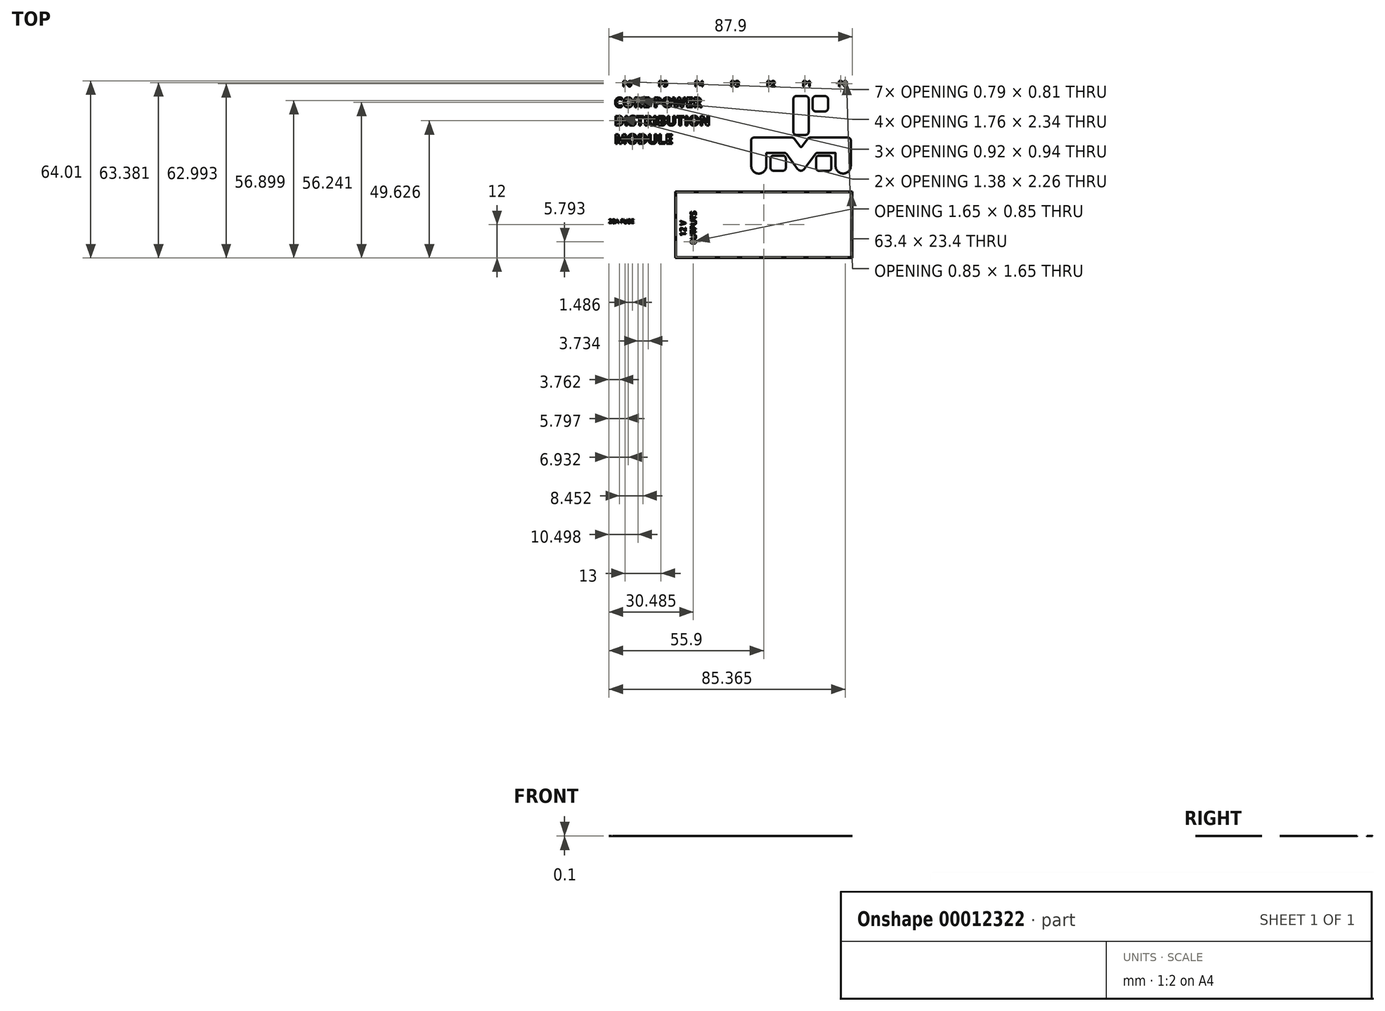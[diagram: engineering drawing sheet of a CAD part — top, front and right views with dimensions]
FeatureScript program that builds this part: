
annotation { "Feature Type Name" : "Feature", "Feature Type Description" : "" }
export const myFeature = defineFeature(function(context is Context, id is Id, definition is map)
    precondition{}
    {
        {
            var Q0;
            Q0=qCreatedBy(makeId("Top.planeOp"),FACE);
            var sketch = newSketch(context, id + "F0", { "sketchPlane" : qUnion([Q0])});
            skText(sketch, "E0", { "text": "P6", "fontName": "OpenSans-Regular.ttf"});
            skPoint(sketch, "E1", {"position": v(0, -2) * mm});
            skPoint(sketch, "E2.1.0.0", {"position": v(13, -2) * mm});
            skPoint(sketch, "E2.2.0.0", {"position": v(26, -2) * mm});
            skPoint(sketch, "E2.3.0.0", {"position": v(39, -2) * mm});
            skPoint(sketch, "E2.4.0.0", {"position": v(52, -2) * mm});
            skPoint(sketch, "E2.5.0.0", {"position": v(65, -2) * mm});
            skPoint(sketch, "E2.6.0.0", {"position": v(78, -2) * mm});
            skLineSegment(sketch, "E2.direction1", {"start": v(0, -2) * mm, "end": v(13, -2) * mm, "construction": true});
            skText(sketch, "E3", { "text": "P5", "fontName": "OpenSans-Regular.ttf"});
            skText(sketch, "E4", { "text": "P4", "fontName": "OpenSans-Regular.ttf"});
            skText(sketch, "E5", { "text": "P3", "fontName": "OpenSans-Regular.ttf"});
            skText(sketch, "E6", { "text": "P2", "fontName": "OpenSans-Regular.ttf"});
            skText(sketch, "E7", { "text": "P1", "fontName": "OpenSans-Regular.ttf"});
            skText(sketch, "E8", { "text": "P0", "fontName": "OpenSans-Regular.ttf"});
            skText(sketch, "E9", { "text": "CORE POWER\nDISTRIBUTION\nMODULE", "fontName": "OpenSans-Bold.ttf"});
            skLineSegment(sketch, "E10.bottom", {"start": v(62.75, -5.5) * mm, "end": v(66.25, -5.5) * mm});
            skLineSegment(sketch, "E10.top", {"start": v(62.75, -19.5) * mm, "end": v(66.25, -19.5) * mm});
            skLineSegment(sketch, "E10.left", {"start": v(61.75, -6.5) * mm, "end": v(61.75, -18.5) * mm});
            skLineSegment(sketch, "E10.right", {"start": v(67.25, -6.5) * mm, "end": v(67.25, -18.5) * mm});
            skLineSegment(sketch, "E11.bottom", {"start": v(69.75, -5.5) * mm, "end": v(73.25, -5.5) * mm});
            skLineSegment(sketch, "E11.top", {"start": v(69.75, -11) * mm, "end": v(73.25, -11) * mm});
            skLineSegment(sketch, "E11.left", {"start": v(68.75, -6.5) * mm, "end": v(68.75, -10) * mm});
            skLineSegment(sketch, "E11.right", {"start": v(74.25, -6.5) * mm, "end": v(74.25, -10) * mm});
            skLineSegment(sketch, "E12", {"start": v(64.5, -19.5) * mm, "end": v(64.5, -33.5) * mm, "construction": true});
            skLineSegment(sketch, "E13", {"start": v(63.3, -31.86) * mm, "end": v(59.27, -26.4) * mm});
            skLineSegment(sketch, "E14", {"start": v(58.47, -26) * mm, "end": v(52.1, -26) * mm});
            skLineSegment(sketch, "E15", {"start": v(52, -26.1) * mm, "end": v(52, -30.75) * mm});
            skLineSegment(sketch, "E16.0", {"start": v(46.5, -21.5) * mm, "end": v(46.5, -30.75) * mm});
            skLineSegment(sketch, "E16.1", {"start": v(61.24, -20.5) * mm, "end": v(47.5, -20.5) * mm});
            skLineSegment(sketch, "E16.2", {"start": v(64.1, -23.68) * mm, "end": v(62.05, -20.9) * mm});
            skLineSegment(sketch, "E17", {"start": v(49.25, -33.5) * mm, "end": v(49.25, -33.5) * mm});
            skPoint(sketch, "E18.orphan", {"position": v(52, -33.5) * mm});
            skPoint(sketch, "E19.visualSharp", {"position": v(46.5, -33.5) * mm});
            skArc(sketch, "E19.filletArc", {"start": v(46.5, -30.75) * mm, "mid": v(47.3, -32.7) * mm, "end": v(49.25, -33.5) * mm});
            skArc(sketch, "E20.filletArc", {"start": v(49.25, -33.5) * mm, "mid": v(51.2, -32.7) * mm, "end": v(52, -30.75) * mm});
            skLineSegment(sketch, "E21.right", {"start": v(59, -28) * mm, "end": v(59, -31.5) * mm});
            skLineSegment(sketch, "E21.left", {"start": v(53.5, -28) * mm, "end": v(53.5, -31.5) * mm});
            skLineSegment(sketch, "E21.top", {"start": v(54.5, -32.5) * mm, "end": v(58, -32.5) * mm});
            skLineSegment(sketch, "E21.bottom", {"start": v(54.5, -27) * mm, "end": v(58, -27) * mm});
            skPoint(sketch, "E22.0.MirrorP", {"position": v(77, -33.5) * mm});
            skLineSegment(sketch, "E22.1.MirrorCS", {"start": v(74.5, -27) * mm, "end": v(71, -27) * mm});
            skPoint(sketch, "E22.2.MirrorP", {"position": v(82.5, -33.5) * mm});
            skLineSegment(sketch, "E22.3.MirrorCS", {"start": v(70, -28) * mm, "end": v(70, -31.5) * mm});
            skLineSegment(sketch, "E22.4.MirrorCS", {"start": v(75.5, -28) * mm, "end": v(75.5, -31.5) * mm});
            skLineSegment(sketch, "E22.5.MirrorCS", {"start": v(74.5, -32.5) * mm, "end": v(71, -32.5) * mm});
            skLineSegment(sketch, "E22.6.MirrorCS", {"start": v(70.53, -26) * mm, "end": v(76.9, -26) * mm});
            skLineSegment(sketch, "E22.7.MirrorCS", {"start": v(77, -26.1) * mm, "end": v(77, -30.75) * mm});
            skArc(sketch, "E22.8.MirrorCS", {"start": v(79.75, -33.5) * mm, "mid": v(77.8, -32.7) * mm, "end": v(77, -30.75) * mm});
            skLineSegment(sketch, "E22.9.MirrorCS", {"start": v(79.75, -33.5) * mm, "end": v(79.75, -33.5) * mm});
            skLineSegment(sketch, "E22.10.MirrorCS", {"start": v(67.76, -20.5) * mm, "end": v(81.5, -20.5) * mm});
            skPoint(sketch, "E22.11.MirrorP", {"position": v(77, -33.5) * mm});
            skLineSegment(sketch, "E22.12.MirrorCS", {"start": v(64.9, -23.68) * mm, "end": v(66.95, -20.9) * mm});
            skArc(sketch, "E22.13.MirrorCS", {"start": v(82.5, -30.75) * mm, "mid": v(81.7, -32.7) * mm, "end": v(79.75, -33.5) * mm});
            skLineSegment(sketch, "E22.14.MirrorCS", {"start": v(65.7, -31.86) * mm, "end": v(69.73, -26.4) * mm});
            skLineSegment(sketch, "E22.15.MirrorCS", {"start": v(82.5, -21.5) * mm, "end": v(82.5, -30.75) * mm});
            skPoint(sketch, "E23.visualSharp", {"position": v(68.75, -5.5) * mm});
            skArc(sketch, "E23.filletArc", {"start": v(69.75, -5.5) * mm, "mid": v(69.04, -5.8) * mm, "end": v(68.75, -6.5) * mm});
            skPoint(sketch, "E24.visualSharp", {"position": v(74.25, -5.5) * mm});
            skArc(sketch, "E24.filletArc", {"start": v(74.25, -6.5) * mm, "mid": v(73.96, -5.8) * mm, "end": v(73.25, -5.5) * mm});
            skPoint(sketch, "E25.visualSharp", {"position": v(74.25, -11) * mm});
            skArc(sketch, "E25.filletArc", {"start": v(73.25, -11) * mm, "mid": v(73.96, -10.7) * mm, "end": v(74.25, -10) * mm});
            skPoint(sketch, "E26.visualSharp", {"position": v(68.75, -11) * mm});
            skArc(sketch, "E26.filletArc", {"start": v(68.75, -10) * mm, "mid": v(69.04, -10.7) * mm, "end": v(69.75, -11) * mm});
            skPoint(sketch, "E27.visualSharp", {"position": v(67.25, -5.5) * mm});
            skArc(sketch, "E27.filletArc", {"start": v(67.25, -6.5) * mm, "mid": v(66.96, -5.8) * mm, "end": v(66.25, -5.5) * mm});
            skPoint(sketch, "E28.visualSharp", {"position": v(61.75, -5.5) * mm});
            skArc(sketch, "E28.filletArc", {"start": v(62.75, -5.5) * mm, "mid": v(62.04, -5.8) * mm, "end": v(61.75, -6.5) * mm});
            skPoint(sketch, "E29.visualSharp", {"position": v(61.75, -19.5) * mm});
            skArc(sketch, "E29.filletArc", {"start": v(61.75, -18.5) * mm, "mid": v(62.04, -19.2) * mm, "end": v(62.75, -19.5) * mm});
            skPoint(sketch, "E30.visualSharp", {"position": v(67.25, -19.5) * mm});
            skArc(sketch, "E30.filletArc", {"start": v(66.25, -19.5) * mm, "mid": v(66.96, -19.2) * mm, "end": v(67.25, -18.5) * mm});
            skPoint(sketch, "E31.visualSharp", {"position": v(70, -32.5) * mm});
            skArc(sketch, "E31.filletArc", {"start": v(70, -31.5) * mm, "mid": v(70.3, -32.2) * mm, "end": v(71, -32.5) * mm});
            skPoint(sketch, "E32.visualSharp", {"position": v(75.5, -27) * mm});
            skArc(sketch, "E32.filletArc", {"start": v(75.5, -28) * mm, "mid": v(75.2, -27.3) * mm, "end": v(74.5, -27) * mm});
            skPoint(sketch, "E33.visualSharp", {"position": v(70, -27) * mm});
            skArc(sketch, "E33.filletArc", {"start": v(71, -27) * mm, "mid": v(70.3, -27.3) * mm, "end": v(70, -28) * mm});
            skPoint(sketch, "E34.visualSharp", {"position": v(75.5, -32.5) * mm});
            skArc(sketch, "E34.filletArc", {"start": v(74.5, -32.5) * mm, "mid": v(75.2, -32.2) * mm, "end": v(75.5, -31.5) * mm});
            skPoint(sketch, "E35.visualSharp", {"position": v(59, -32.5) * mm});
            skArc(sketch, "E35.filletArc", {"start": v(58, -32.5) * mm, "mid": v(58.7, -32.2) * mm, "end": v(59, -31.5) * mm});
            skPoint(sketch, "E36.visualSharp", {"position": v(59, -27) * mm});
            skArc(sketch, "E36.filletArc", {"start": v(59, -28) * mm, "mid": v(58.7, -27.3) * mm, "end": v(58, -27) * mm});
            skPoint(sketch, "E37.visualSharp", {"position": v(53.5, -27) * mm});
            skArc(sketch, "E37.filletArc", {"start": v(54.5, -27) * mm, "mid": v(53.8, -27.3) * mm, "end": v(53.5, -28) * mm});
            skPoint(sketch, "E38.visualSharp", {"position": v(53.5, -32.5) * mm});
            skArc(sketch, "E38.filletArc", {"start": v(53.5, -31.5) * mm, "mid": v(53.8, -32.2) * mm, "end": v(54.5, -32.5) * mm});
            skPoint(sketch, "E39.visualSharp", {"position": v(46.5, -20.5) * mm});
            skArc(sketch, "E39.filletArc", {"start": v(47.5, -20.5) * mm, "mid": v(46.8, -20.8) * mm, "end": v(46.5, -21.5) * mm});
            skPoint(sketch, "E40.visualSharp", {"position": v(82.5, -20.5) * mm});
            skArc(sketch, "E40.filletArc", {"start": v(82.5, -21.5) * mm, "mid": v(82.2, -20.8) * mm, "end": v(81.5, -20.5) * mm});
            skPoint(sketch, "E41.visualSharp", {"position": v(61.75, -20.5) * mm});
            skArc(sketch, "E41.filletArc", {"start": v(62.05, -20.9) * mm, "mid": v(61.7, -20.6) * mm, "end": v(61.24, -20.5) * mm});
            skPoint(sketch, "E42.visualSharp", {"position": v(67.25, -20.5) * mm});
            skArc(sketch, "E42.filletArc", {"start": v(67.76, -20.5) * mm, "mid": v(67.3, -20.6) * mm, "end": v(66.95, -20.9) * mm});
            skPoint(sketch, "E43.visualSharp", {"position": v(52, -26) * mm});
            skArc(sketch, "E43.filletArc", {"start": v(52.1, -26) * mm, "mid": v(52.03, -26.03) * mm, "end": v(52, -26.1) * mm});
            skPoint(sketch, "E44.visualSharp", {"position": v(77, -26) * mm});
            skArc(sketch, "E44.filletArc", {"start": v(77, -26.1) * mm, "mid": v(76.97, -26.03) * mm, "end": v(76.9, -26) * mm});
            skPoint(sketch, "E45.visualSharp", {"position": v(70.03, -26) * mm});
            skArc(sketch, "E45.filletArc", {"start": v(70.53, -26) * mm, "mid": v(70.08, -26.1) * mm, "end": v(69.73, -26.4) * mm});
            skPoint(sketch, "E46.visualSharp", {"position": v(58.97, -26) * mm});
            skArc(sketch, "E46.filletArc", {"start": v(59.27, -26.4) * mm, "mid": v(58.92, -26.1) * mm, "end": v(58.47, -26) * mm});
            skPoint(sketch, "E47.visualSharp", {"position": v(64.5, -33.5) * mm});
            skArc(sketch, "E47.filletArc", {"start": v(63.3, -31.86) * mm, "mid": v(64.5, -32.47) * mm, "end": v(65.7, -31.86) * mm});
            skPoint(sketch, "E48.visualSharp", {"position": v(64.5, -24.23) * mm});
            skArc(sketch, "E48.filletArc", {"start": v(64.1, -23.68) * mm, "mid": v(64.5, -23.89) * mm, "end": v(64.9, -23.68) * mm});
            skText(sketch, "E49", { "text": "20A FUSE\n", "fontName": "OpenSans-Regular.ttf"});
            skLineSegment(sketch, "E50.bottom", {"start": v(19, -40) * mm, "end": v(83, -40) * mm});
            skLineSegment(sketch, "E50.top", {"start": v(19, -64) * mm, "end": v(83, -64) * mm});
            skLineSegment(sketch, "E50.left", {"start": v(19, -40) * mm, "end": v(19, -64) * mm});
            skLineSegment(sketch, "E50.right", {"start": v(83, -40) * mm, "end": v(83, -64) * mm});
            skLineSegment(sketch, "E51.0", {"start": v(19.3, -40.3) * mm, "end": v(82.7, -40.3) * mm});
            skLineSegment(sketch, "E51.1", {"start": v(19.3, -40.3) * mm, "end": v(19.3, -63.7) * mm});
            skLineSegment(sketch, "E51.2", {"start": v(19.3, -63.7) * mm, "end": v(82.7, -63.7) * mm});
            skLineSegment(sketch, "E51.3", {"start": v(82.7, -40.3) * mm, "end": v(82.7, -63.7) * mm});
            skText(sketch, "E52", { "text": "    12 V\n0UTPUTS", "fontName": "OpenSans-Regular.ttf"});
            const initialGuessF0  = {"E0": [0, -0.002, 1, 0, 0.002], "E3": [0.013, -0.002, 1, 0, 0.002], "E4": [0.026, -0.002, 1, 0, 0.002], "E5": [0.039, -0.002, 1, 0, 0.002], "E6": [0.052, -0.002, 1, 0, 0.002], "E7": [0.065, -0.002, 1, 0, 0.002], "E8": [0.078, -0.002, 1, 0, 0.002], "E9": [-0.003, -0.0095, 1, 0, 0.0035], "E49": [-0.005, -0.0515, 1, 0, 0.0015], "E52": [0.0228, -0.059, 0, 1, 0.002]};
            skSetInitialGuess(sketch, initialGuessF0);
            skSolve(sketch);
        }
        {
            var Q0;
            Q0=makeQuery(id+"F0.imprint","IMPRINT",FACE,{"disambiguationData":[TD([[makeQuery(id+"F0.imprint","IMPRINT",EDGE,{"derivedFrom":sQuery(id+"F0.wireOp",EDGE,"E3.sketch_text.stroke-15")}),-1.0]])]});
            var Q1;
            Q1=makeQuery(id+"F0.imprint","IMPRINT",FACE,{"disambiguationData":[TD([[makeQuery(id+"F0.imprint","IMPRINT",EDGE,{"derivedFrom":sQuery(id+"F0.wireOp",EDGE,"E5.sketch_text.stroke-15")}),-1.0]])]});
            var Q2;
            Q2=makeQuery(id+"F0.imprint","IMPRINT",FACE,{"disambiguationData":[TD([[makeQuery(id+"F0.imprint","IMPRINT",EDGE,{"derivedFrom":sQuery(id+"F0.wireOp",EDGE,"E6.sketch_text.stroke-15")}),-1.0]])]});
            var Q3;
            Q3=makeQuery(id+"F0.imprint","IMPRINT",FACE,{"disambiguationData":[TD([[makeQuery(id+"F0.imprint","IMPRINT",EDGE,{"derivedFrom":sQuery(id+"F0.wireOp",EDGE,"E7.sketch_text.stroke-15")}),-1.0]])]});
            var Q4;
            Q4=makeQuery(id+"F0.imprint","IMPRINT",FACE,{"disambiguationData":[TD([[makeQuery(id+"F0.imprint","IMPRINT",EDGE,{"derivedFrom":sQuery(id+"F0.wireOp",EDGE,"E9.sketch_text.stroke-0")}),-1.0]])]});
            var Q5;
            Q5=makeQuery(id+"F0.imprint","IMPRINT",FACE,{"disambiguationData":[TD([[makeQuery(id+"F0.imprint","IMPRINT",EDGE,{"derivedFrom":sQuery(id+"F0.wireOp",EDGE,"E9.sketch_text.stroke-48")}),-1.0]])]});
            var Q6;
            Q6=makeQuery(id+"F0.imprint","IMPRINT",FACE,{"disambiguationData":[TD([[makeQuery(id+"F0.imprint","IMPRINT",EDGE,{"derivedFrom":sQuery(id+"F0.wireOp",EDGE,"E9.sketch_text.stroke-90")}),-1.0]])]});
            var Q7;
            Q7=makeQuery(id+"F0.imprint","IMPRINT",FACE,{"disambiguationData":[TD([[makeQuery(id+"F0.imprint","IMPRINT",EDGE,{"derivedFrom":sQuery(id+"F0.wireOp",EDGE,"E9.sketch_text.stroke-114")}),-1.0]])]});
            var Q8;
            Q8=makeQuery(id+"F0.imprint","IMPRINT",FACE,{"disambiguationData":[TD([[makeQuery(id+"F0.imprint","IMPRINT",EDGE,{"derivedFrom":sQuery(id+"F0.wireOp",EDGE,"E9.sketch_text.stroke-157")}),-1.0]])]});
            var Q9;
            Q9=makeQuery(id+"F0.imprint","IMPRINT",FACE,{"disambiguationData":[TD([[makeQuery(id+"F0.imprint","IMPRINT",EDGE,{"derivedFrom":sQuery(id+"F0.wireOp",EDGE,"E9.sketch_text.stroke-161")}),-1.0]])]});
            var Q10;
            Q10=makeQuery(id+"F0.imprint","IMPRINT",FACE,{"disambiguationData":[TD([[makeQuery(id+"F0.imprint","IMPRINT",EDGE,{"derivedFrom":sQuery(id+"F0.wireOp",EDGE,"E9.sketch_text.stroke-189")}),-1.0]])]});
            var Q11;
            Q11=makeQuery(id+"F0.imprint","IMPRINT",FACE,{"disambiguationData":[TD([[makeQuery(id+"F0.imprint","IMPRINT",EDGE,{"derivedFrom":sQuery(id+"F0.wireOp",EDGE,"E9.sketch_text.stroke-216")}),-1.0]])]});
            var Q12;
            Q12=makeQuery(id+"F0.imprint","IMPRINT",FACE,{"disambiguationData":[TD([[makeQuery(id+"F0.imprint","IMPRINT",EDGE,{"derivedFrom":sQuery(id+"F0.wireOp",EDGE,"E9.sketch_text.stroke-245")}),-1.0]])]});
            var Q13;
            Q13=makeQuery(id+"F0.imprint","IMPRINT",FACE,{"disambiguationData":[TD([[makeQuery(id+"F0.imprint","IMPRINT",EDGE,{"derivedFrom":sQuery(id+"F0.wireOp",EDGE,"E9.sketch_text.stroke-260")}),-1.0]])]});
            var Q14;
            Q14=makeQuery(id+"F0.imprint","IMPRINT",FACE,{"disambiguationData":[TD([[makeQuery(id+"F0.imprint","IMPRINT",EDGE,{"derivedFrom":sQuery(id+"F0.wireOp",EDGE,"E9.sketch_text.stroke-268")}),-1.0]])]});
            var Q15;
            Q15=makeQuery(id+"F0.imprint","IMPRINT",FACE,{"disambiguationData":[TD([[makeQuery(id+"F0.imprint","IMPRINT",EDGE,{"derivedFrom":sQuery(id+"F0.wireOp",EDGE,"E9.sketch_text.stroke-286")}),-1.0]])]});
            var Q16;
            Q16=makeQuery(id+"F0.imprint","IMPRINT",FACE,{"disambiguationData":[TD([[makeQuery(id+"F0.imprint","IMPRINT",EDGE,{"derivedFrom":sQuery(id+"F0.wireOp",EDGE,"E9.sketch_text.stroke-300")}),-1.0]])]});
            var Q17;
            Q17=makeQuery(id+"F0.imprint","IMPRINT",FACE,{"disambiguationData":[TD([[makeQuery(id+"F0.imprint","IMPRINT",EDGE,{"derivedFrom":sQuery(id+"F0.wireOp",EDGE,"E9.sketch_text.stroke-345")}),-1.0]])]});
            var Q18;
            Q18=makeQuery(id+"F0.imprint","IMPRINT",FACE,{"disambiguationData":[TD([[makeQuery(id+"F0.imprint","IMPRINT",EDGE,{"derivedFrom":sQuery(id+"F0.wireOp",EDGE,"E9.sketch_text.stroke-360")}),-1.0]])]});
            var Q19;
            Q19=makeQuery(id+"F0.imprint","IMPRINT",FACE,{"disambiguationData":[TD([[makeQuery(id+"F0.imprint","IMPRINT",EDGE,{"derivedFrom":sQuery(id+"F0.wireOp",EDGE,"E9.sketch_text.stroke-366")}),-1.0]])]});
            var Q20;
            Q20=makeQuery(id+"F0.imprint","IMPRINT",FACE,{"disambiguationData":[TD([[makeQuery(id+"F0.imprint","IMPRINT",EDGE,{"derivedFrom":sQuery(id+"F0.wireOp",EDGE,"E10.bottom")}),-1.0]])]});
            var Q21;
            Q21=makeQuery(id+"F0.imprint","IMPRINT",FACE,{"disambiguationData":[TD([[makeQuery(id+"F0.imprint","IMPRINT",EDGE,{"derivedFrom":sQuery(id+"F0.wireOp",EDGE,"E11.bottom")}),-1.0]])]});
            var Q22;
            Q22=makeQuery(id+"F0.imprint","IMPRINT",FACE,{"disambiguationData":[TD([[makeQuery(id+"F0.imprint","IMPRINT",EDGE,{"derivedFrom":sQuery(id+"F0.wireOp",EDGE,"E13")}),-1.0]])]});
            var Q23;
            Q23=makeQuery(id+"F0.imprint","IMPRINT",FACE,{"disambiguationData":[TD([[makeQuery(id+"F0.imprint","IMPRINT",EDGE,{"derivedFrom":sQuery(id+"F0.wireOp",EDGE,"E21.right")}),-1.0]])]});
            var Q24;
            Q24=makeQuery(id+"F0.imprint","IMPRINT",FACE,{"disambiguationData":[TD([[makeQuery(id+"F0.imprint","IMPRINT",EDGE,{"derivedFrom":sQuery(id+"F0.wireOp",EDGE,"E22.1.MirrorCS")}),1.0]])]});
            var Q25;
            Q25=makeQuery(id+"F0.imprint","IMPRINT",FACE,{"disambiguationData":[TD([[makeQuery(id+"F0.imprint","IMPRINT",EDGE,{"derivedFrom":sQuery(id+"F0.wireOp",EDGE,"E49.sketch_text.stroke-0")}),-1.0]])]});
            var Q26;
            Q26=makeQuery(id+"F0.imprint","IMPRINT",FACE,{"disambiguationData":[TD([[makeQuery(id+"F0.imprint","IMPRINT",EDGE,{"derivedFrom":sQuery(id+"F0.wireOp",EDGE,"E49.sketch_text.stroke-49")}),-1.0]])]});
            var Q27;
            Q27=makeQuery(id+"F0.imprint","IMPRINT",FACE,{"disambiguationData":[TD([[makeQuery(id+"F0.imprint","IMPRINT",EDGE,{"derivedFrom":sQuery(id+"F0.wireOp",EDGE,"E49.sketch_text.stroke-59")}),-1.0]])]});
            var Q28;
            Q28=makeQuery(id+"F0.imprint","IMPRINT",FACE,{"disambiguationData":[TD([[makeQuery(id+"F0.imprint","IMPRINT",EDGE,{"derivedFrom":sQuery(id+"F0.wireOp",EDGE,"E49.sketch_text.stroke-73")}),-1.0]])]});
            var Q29;
            Q29=makeQuery(id+"F0.imprint","IMPRINT",FACE,{"disambiguationData":[TD([[makeQuery(id+"F0.imprint","IMPRINT",EDGE,{"derivedFrom":sQuery(id+"F0.wireOp",EDGE,"E49.sketch_text.stroke-98")}),-1.0]])]});
            var Q30;
            Q30=makeQuery(id+"F0.imprint","IMPRINT",FACE,{"disambiguationData":[TD([[makeQuery(id+"F0.imprint","IMPRINT",EDGE,{"derivedFrom":sQuery(id+"F0.wireOp",EDGE,"E0.sketch_text.stroke-0")}),-1.0]])]});
            var Q31;
            Q31=makeQuery(id+"F0.imprint","IMPRINT",FACE,{"disambiguationData":[TD([[makeQuery(id+"F0.imprint","IMPRINT",EDGE,{"derivedFrom":sQuery(id+"F0.wireOp",EDGE,"E0.sketch_text.stroke-15")}),-1.0]])]});
            var Q32;
            Q32=makeQuery(id+"F0.imprint","IMPRINT",FACE,{"disambiguationData":[TD([[makeQuery(id+"F0.imprint","IMPRINT",EDGE,{"derivedFrom":sQuery(id+"F0.wireOp",EDGE,"E3.sketch_text.stroke-0")}),-1.0]])]});
            var Q33;
            Q33=makeQuery(id+"F0.imprint","IMPRINT",FACE,{"disambiguationData":[TD([[makeQuery(id+"F0.imprint","IMPRINT",EDGE,{"derivedFrom":sQuery(id+"F0.wireOp",EDGE,"E4.sketch_text.stroke-0")}),-1.0]])]});
            var Q34;
            Q34=makeQuery(id+"F0.imprint","IMPRINT",FACE,{"disambiguationData":[TD([[makeQuery(id+"F0.imprint","IMPRINT",EDGE,{"derivedFrom":sQuery(id+"F0.wireOp",EDGE,"E4.sketch_text.stroke-15")}),-1.0]])]});
            var Q35;
            Q35=makeQuery(id+"F0.imprint","IMPRINT",FACE,{"disambiguationData":[TD([[makeQuery(id+"F0.imprint","IMPRINT",EDGE,{"derivedFrom":sQuery(id+"F0.wireOp",EDGE,"E5.sketch_text.stroke-0")}),-1.0]])]});
            var Q36;
            Q36=makeQuery(id+"F0.imprint","IMPRINT",FACE,{"disambiguationData":[TD([[makeQuery(id+"F0.imprint","IMPRINT",EDGE,{"derivedFrom":sQuery(id+"F0.wireOp",EDGE,"E6.sketch_text.stroke-0")}),-1.0]])]});
            var Q37;
            Q37=makeQuery(id+"F0.imprint","IMPRINT",FACE,{"disambiguationData":[TD([[makeQuery(id+"F0.imprint","IMPRINT",EDGE,{"derivedFrom":sQuery(id+"F0.wireOp",EDGE,"E7.sketch_text.stroke-0")}),-1.0]])]});
            var Q38;
            Q38=makeQuery(id+"F0.imprint","IMPRINT",FACE,{"disambiguationData":[TD([[makeQuery(id+"F0.imprint","IMPRINT",EDGE,{"derivedFrom":sQuery(id+"F0.wireOp",EDGE,"E8.sketch_text.stroke-0")}),-1.0]])]});
            var Q39;
            Q39=makeQuery(id+"F0.imprint","IMPRINT",FACE,{"disambiguationData":[TD([[makeQuery(id+"F0.imprint","IMPRINT",EDGE,{"derivedFrom":sQuery(id+"F0.wireOp",EDGE,"E8.sketch_text.stroke-15")}),-1.0]])]});
            var Q40;
            Q40=makeQuery(id+"F0.imprint","IMPRINT",FACE,{"disambiguationData":[TD([[makeQuery(id+"F0.imprint","IMPRINT",EDGE,{"derivedFrom":sQuery(id+"F0.wireOp",EDGE,"E9.sketch_text.stroke-15")}),-1.0]])]});
            var Q41;
            Q41=makeQuery(id+"F0.imprint","IMPRINT",FACE,{"disambiguationData":[TD([[makeQuery(id+"F0.imprint","IMPRINT",EDGE,{"derivedFrom":sQuery(id+"F0.wireOp",EDGE,"E9.sketch_text.stroke-29")}),-1.0]])]});
            var Q42;
            Q42=makeQuery(id+"F0.imprint","IMPRINT",FACE,{"disambiguationData":[TD([[makeQuery(id+"F0.imprint","IMPRINT",EDGE,{"derivedFrom":sQuery(id+"F0.wireOp",EDGE,"E9.sketch_text.stroke-60")}),-1.0]])]});
            var Q43;
            Q43=makeQuery(id+"F0.imprint","IMPRINT",FACE,{"disambiguationData":[TD([[makeQuery(id+"F0.imprint","IMPRINT",EDGE,{"derivedFrom":sQuery(id+"F0.wireOp",EDGE,"E9.sketch_text.stroke-76")}),-1.0]])]});
            var Q44;
            Q44=makeQuery(id+"F0.imprint","IMPRINT",FACE,{"disambiguationData":[TD([[makeQuery(id+"F0.imprint","IMPRINT",EDGE,{"derivedFrom":sQuery(id+"F0.wireOp",EDGE,"E9.sketch_text.stroke-126")}),-1.0]])]});
            var Q45;
            Q45=makeQuery(id+"F0.imprint","IMPRINT",FACE,{"disambiguationData":[TD([[makeQuery(id+"F0.imprint","IMPRINT",EDGE,{"derivedFrom":sQuery(id+"F0.wireOp",EDGE,"E9.sketch_text.stroke-145")}),-1.0]])]});
            var Q46;
            Q46=makeQuery(id+"F0.imprint","IMPRINT",FACE,{"disambiguationData":[TD([[makeQuery(id+"F0.imprint","IMPRINT",EDGE,{"derivedFrom":sQuery(id+"F0.wireOp",EDGE,"E9.sketch_text.stroke-197")}),-1.0]])]});
            var Q47;
            Q47=makeQuery(id+"F0.imprint","IMPRINT",FACE,{"disambiguationData":[TD([[makeQuery(id+"F0.imprint","IMPRINT",EDGE,{"derivedFrom":sQuery(id+"F0.wireOp",EDGE,"E9.sketch_text.stroke-272")}),-1.0]])]});
            var Q48;
            Q48=makeQuery(id+"F0.imprint","IMPRINT",FACE,{"disambiguationData":[TD([[makeQuery(id+"F0.imprint","IMPRINT",EDGE,{"derivedFrom":sQuery(id+"F0.wireOp",EDGE,"E9.sketch_text.stroke-319")}),-1.0]])]});
            var Q49;
            Q49=makeQuery(id+"F0.imprint","IMPRINT",FACE,{"disambiguationData":[TD([[makeQuery(id+"F0.imprint","IMPRINT",EDGE,{"derivedFrom":sQuery(id+"F0.wireOp",EDGE,"E9.sketch_text.stroke-333")}),-1.0]])]});
            var Q50;
            Q50=makeQuery(id+"F0.imprint","IMPRINT",FACE,{"disambiguationData":[TD([[makeQuery(id+"F0.imprint","IMPRINT",EDGE,{"derivedFrom":sQuery(id+"F0.wireOp",EDGE,"E49.sketch_text.stroke-20")}),-1.0]])]});
            var Q51;
            Q51=makeQuery(id+"F0.imprint","IMPRINT",FACE,{"disambiguationData":[TD([[makeQuery(id+"F0.imprint","IMPRINT",EDGE,{"derivedFrom":sQuery(id+"F0.wireOp",EDGE,"E49.sketch_text.stroke-36")}),-1.0]])]});
            var Q52;
            Q52=makeQuery(id+"F0.imprint","IMPRINT",FACE,{"disambiguationData":[TD([[makeQuery(id+"F0.imprint","IMPRINT",EDGE,{"derivedFrom":sQuery(id+"F0.wireOp",EDGE,"E50.bottom")}),-1.0]])]});
            var Q53;
            Q53=makeQuery(id+"F0.imprint","IMPRINT",FACE,{"disambiguationData":[TD([[makeQuery(id+"F0.imprint","IMPRINT",EDGE,{"derivedFrom":sQuery(id+"F0.wireOp",EDGE,"E9.sketch_text.stroke-220")}),-1.0]])]});
            var Q54;
            Q54=makeQuery(id+"F0.imprint","IMPRINT",FACE,{"disambiguationData":[TD([[makeQuery(id+"F0.imprint","IMPRINT",EDGE,{"derivedFrom":sQuery(id+"F0.wireOp",EDGE,"E52.sketch_text.stroke-29")}),-1.0]])]});
            var Q55;
            Q55=makeQuery(id+"F0.imprint","IMPRINT",FACE,{"disambiguationData":[TD([[makeQuery(id+"F0.imprint","IMPRINT",EDGE,{"derivedFrom":sQuery(id+"F0.wireOp",EDGE,"E52.sketch_text.stroke-113")}),-1.0]])]});
            var Q56;
            Q56=makeQuery(id+"F0.imprint","IMPRINT",FACE,{"disambiguationData":[TD([[makeQuery(id+"F0.imprint","IMPRINT",EDGE,{"derivedFrom":sQuery(id+"F0.wireOp",EDGE,"E52.sketch_text.stroke-38")}),-1.0]])]});
            var Q57;
            Q57=makeQuery(id+"F0.imprint","IMPRINT",FACE,{"disambiguationData":[TD([[makeQuery(id+"F0.imprint","IMPRINT",EDGE,{"derivedFrom":sQuery(id+"F0.wireOp",EDGE,"E52.sketch_text.stroke-91")}),-1.0]])]});
            var Q58;
            Q58=makeQuery(id+"F0.imprint","IMPRINT",FACE,{"disambiguationData":[TD([[makeQuery(id+"F0.imprint","IMPRINT",EDGE,{"derivedFrom":sQuery(id+"F0.wireOp",EDGE,"E52.sketch_text.stroke-105")}),-1.0]])]});
            var Q59;
            Q59=makeQuery(id+"F0.imprint","IMPRINT",FACE,{"disambiguationData":[TD([[makeQuery(id+"F0.imprint","IMPRINT",EDGE,{"derivedFrom":sQuery(id+"F0.wireOp",EDGE,"E52.sketch_text.stroke-68")}),-1.0]])]});
            var Q60;
            Q60=makeQuery(id+"F0.imprint","IMPRINT",FACE,{"disambiguationData":[TD([[makeQuery(id+"F0.imprint","IMPRINT",EDGE,{"derivedFrom":sQuery(id+"F0.wireOp",EDGE,"E52.sketch_text.stroke-54")}),-1.0]])]});
            var Q61;
            Q61=makeQuery(id+"F0.imprint","IMPRINT",FACE,{"disambiguationData":[TD([[makeQuery(id+"F0.imprint","IMPRINT",EDGE,{"derivedFrom":sQuery(id+"F0.wireOp",EDGE,"E52.sketch_text.stroke-76")}),-1.0]])]});
            var Q62;
            Q62=makeQuery(id+"F0.imprint","IMPRINT",FACE,{"disambiguationData":[TD([[makeQuery(id+"F0.imprint","IMPRINT",EDGE,{"derivedFrom":sQuery(id+"F0.wireOp",EDGE,"E52.sketch_text.stroke-9")}),-1.0]])]});
            var Q63;
            Q63=makeQuery(id+"F0.imprint","IMPRINT",FACE,{"disambiguationData":[TD([[makeQuery(id+"F0.imprint","IMPRINT",EDGE,{"derivedFrom":sQuery(id+"F0.wireOp",EDGE,"E52.sketch_text.stroke-0")}),-1.0]])]});
            extrude(context, id + "F1", {"entities" : qUnion([Q0, Q1, Q2, Q3, Q4, Q5, Q6, Q7, Q8, Q9, Q10, Q11, Q12, Q13, Q14, Q15, Q16, Q17, Q18, Q19, Q20, Q21, Q22, Q23, Q24, Q25, Q26, Q27, Q28, Q29, Q30, Q31, Q32, Q33, Q34, Q35, Q36, Q37, Q38, Q39, Q40, Q41, Q42, Q43, Q44, Q45, Q46, Q47, Q48, Q49, Q50, Q51, Q52, Q53, Q54, Q55, Q56, Q57, Q58, Q59, Q60, Q61, Q62, Q63]), "depth" : .1 * mm});
        }
    });
